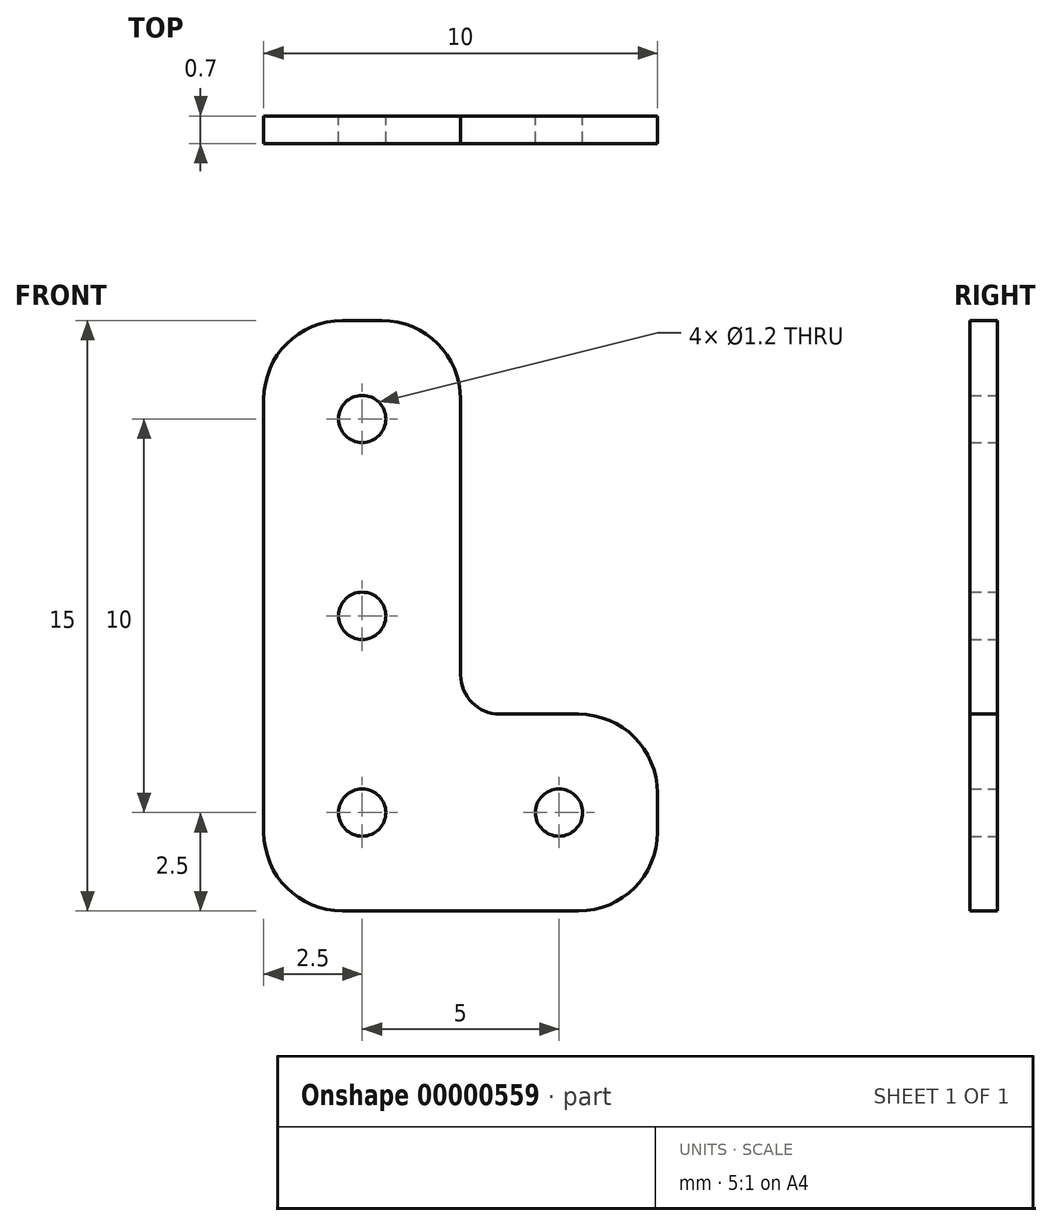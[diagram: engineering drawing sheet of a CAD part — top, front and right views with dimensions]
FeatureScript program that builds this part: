
annotation { "Feature Type Name" : "Feature", "Feature Type Description" : "" }
export const myFeature = defineFeature(function(context is Context, id is Id, definition is map)
    precondition{}
    {
        {
            var Q0;
            Q0=qCreatedBy(makeId("Front.planeOp"),FACE);
            var sketch = newSketch(context, id + "F0", { "sketchPlane" : qUnion([Q0])});
            skLineSegment(sketch, "E0", {"start": v(2, 0) * mm, "end": v(8, 0) * mm});
            skLineSegment(sketch, "E1", {"start": v(10, 2) * mm, "end": v(10, 3) * mm});
            skLineSegment(sketch, "E2", {"start": v(8, 5) * mm, "end": v(6, 5) * mm});
            skLineSegment(sketch, "E3", {"start": v(5, 6) * mm, "end": v(5, 13) * mm});
            skLineSegment(sketch, "E4", {"start": v(3, 15) * mm, "end": v(2, 15) * mm});
            skLineSegment(sketch, "E5", {"start": v(0, 13) * mm, "end": v(0, 2) * mm});
            skCircle(sketch, "E6", {"center": v(2.5, 12.5) * mm, "radius": 0.6 * mm});
            skPoint(sketch, "E7", {"position": v(0, 5) * mm});
            skCircle(sketch, "E8", {"center": v(2.5, 7.5) * mm, "radius": 0.6 * mm});
            skCircle(sketch, "E9", {"center": v(2.5, 2.5) * mm, "radius": 0.6 * mm});
            skCircle(sketch, "E10", {"center": v(7.5, 2.5) * mm, "radius": 0.6 * mm});
            skPoint(sketch, "E11.visualSharp", {"position": v(5, 15) * mm});
            skArc(sketch, "E11.filletArc", {"start": v(5, 13) * mm, "mid": v(4.41, 14.41) * mm, "end": v(3, 15) * mm});
            skPoint(sketch, "E12.visualSharp", {"position": v(10, 5) * mm});
            skArc(sketch, "E12.filletArc", {"start": v(10, 3) * mm, "mid": v(9.41, 4.41) * mm, "end": v(8, 5) * mm});
            skPoint(sketch, "E13.visualSharp", {"position": v(0, 0) * mm});
            skArc(sketch, "E13.filletArc", {"start": v(0, 2) * mm, "mid": v(0.59, 0.59) * mm, "end": v(2, 0) * mm});
            skPoint(sketch, "E14.visualSharp", {"position": v(0, 15) * mm});
            skArc(sketch, "E14.filletArc", {"start": v(2, 15) * mm, "mid": v(0.59, 14.41) * mm, "end": v(0, 13) * mm});
            skPoint(sketch, "E15.visualSharp", {"position": v(10, 0) * mm});
            skArc(sketch, "E15.filletArc", {"start": v(8, 0) * mm, "mid": v(9.41, 0.59) * mm, "end": v(10, 2) * mm});
            skPoint(sketch, "E16.visualSharp", {"position": v(5, 5) * mm});
            skArc(sketch, "E16.filletArc", {"start": v(5, 6) * mm, "mid": v(5.3, 5.3) * mm, "end": v(6, 5) * mm});
            skSolve(sketch);
        }
        {
            var Q0;
            Q0=makeQuery(id+"F0.imprint","IMPRINT",FACE,{"disambiguationData":[TD([[makeQuery(id+"F0.imprint","IMPRINT",EDGE,{"derivedFrom":sQuery(id+"F0.wireOp",EDGE,"E0")}),1.0]])]});
            extrude(context, id + "F1", {"entities" : qUnion([Q0]), "depth" : .7 * mm});
        }
    });
